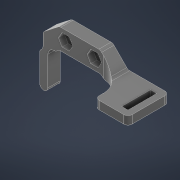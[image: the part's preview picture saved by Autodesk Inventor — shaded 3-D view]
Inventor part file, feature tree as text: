
AUTODESK INVENTOR PART (.ipt)
format: ipt  version: 2021 (Build 250183000, 183)  size: 244,224 bytes
history: native  units: mm
features: reference x10, other x8, extrude x5, fillet x5, plane x1
ambient origin geometry x8: Origin, YZ Plane, XZ Plane, XY Plane, X Axis, Y Axis, Z Axis, Center Point
bodies: Solid1 (feature_tree)
feature tree (29):
  plane  "Work Plane1"
  extrude  "mount"  Depth=20.0mm
  fillet  "common"  Radius=110.0mm
  fillet  "battery_corner"  Radius=6.5mm
  extrude  "nuts"  Depth=27.6mm
  extrude  "wall"  Depth=4.0mm
  fillet  "wall_fillets"  Radius=14.0mm
  extrude  "fastener_slot"  Depth=5.0mm
  fillet  "wall_support"  Radius=19.2mm
  extrude  "steering_column_collision_cutout"  Depth=4.0mm
  fillet  "steering_column_collision_cutout_fillet"  Radius=3.4mm
  other  "mount_sketch"
  reference  "Reference1"
  reference  "Reference2"
  reference  "Reference3"
  reference  "Reference4"
  reference  "Reference5"
  reference  "Reference6"
  reference  "Reference7"
  reference  "Reference8"
  reference  "Reference9"
  reference  "Reference10"
  other  "nuts_sketch"
  other  "wall_sketch"
  other  "fastener_slot_sketch"
  other  "steering_column_collision_cutout_sketch"
  parser-record x1  (decoder bookkeeping rows leaked as tree rows — omitted from the tree; the rows remain in map.json)
  other  "mount_battery.iam"
  other  "base_short:1"
note: 1 file-system path scrubbed to <path> (originals preserved in map.json)
